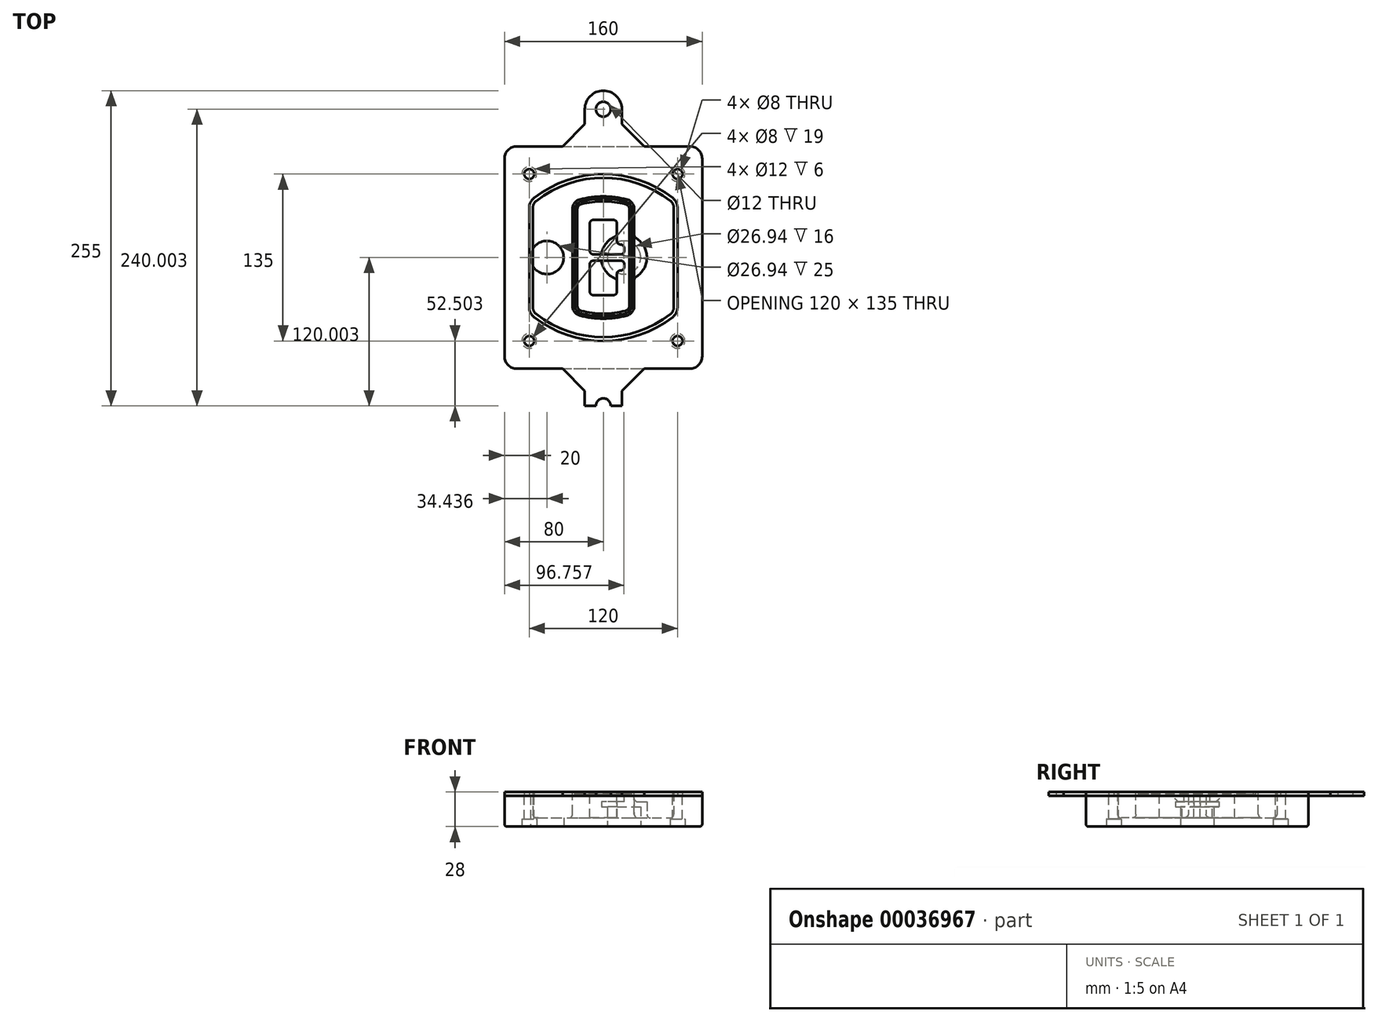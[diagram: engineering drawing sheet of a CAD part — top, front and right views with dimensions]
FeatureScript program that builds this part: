
annotation { "Feature Type Name" : "Feature", "Feature Type Description" : "" }
export const myFeature = defineFeature(function(context is Context, id is Id, definition is map)
    precondition{}
    {
        {
            var Q0;
            Q0=qCreatedBy(makeId("Top.planeOp"),FACE);
            var sketch = newSketch(context, id + "F0", { "sketchPlane" : qUnion([Q0])});
            skPoint(sketch, "E0.rect.middle", {"position": v(0, 0) * mm});
            skLineSegment(sketch, "E1.bottom", {"start": v(24.05, 28.38) * mm, "end": v(164.05, 28.38) * mm});
            skLineSegment(sketch, "E1.top", {"start": v(24.05, 208.38) * mm, "end": v(164.05, 208.38) * mm});
            skLineSegment(sketch, "E1.left", {"start": v(14.05, 38.38) * mm, "end": v(14.05, 198.38) * mm});
            skLineSegment(sketch, "E1.right", {"start": v(174.05, 38.38) * mm, "end": v(174.05, 198.38) * mm});
            skLineSegment(sketch, "E2", {"start": v(14.05, 208.38) * mm, "end": v(174.05, 28.38) * mm, "construction": true});
            skLineSegment(sketch, "E3", {"start": v(174.05, 208.38) * mm, "end": v(14.05, 28.38) * mm, "construction": true});
            skCircle(sketch, "E4", {"center": v(34.05, 185.88) * mm, "radius": 4 * mm});
            skCircle(sketch, "E5", {"center": v(154.05, 185.88) * mm, "radius": 4 * mm});
            skCircle(sketch, "E6", {"center": v(154.05, 50.88) * mm, "radius": 4 * mm});
            skCircle(sketch, "E7", {"center": v(34.05, 50.88) * mm, "radius": 4 * mm});
            skLineSegment(sketch, "E8", {"start": v(34.05, 185.88) * mm, "end": v(154.05, 185.88) * mm, "construction": true});
            skLineSegment(sketch, "E9", {"start": v(154.05, 185.88) * mm, "end": v(154.05, 50.88) * mm, "construction": true});
            skLineSegment(sketch, "E10", {"start": v(154.05, 50.88) * mm, "end": v(34.05, 50.88) * mm, "construction": true});
            skLineSegment(sketch, "E11", {"start": v(34.05, 50.88) * mm, "end": v(34.05, 185.88) * mm, "construction": true});
            skLineSegment(sketch, "E12", {"start": v(34.05, 158.68) * mm, "end": v(34.05, 78.09) * mm});
            skLineSegment(sketch, "E13", {"start": v(154.05, 158.68) * mm, "end": v(154.05, 78.09) * mm});
            skArc(sketch, "E14", {"start": v(150.2, 166.56) * mm, "mid": v(94.05, 185.88) * mm, "end": v(37.9, 166.56) * mm});
            skArc(sketch, "E15", {"start": v(37.9, 70.2) * mm, "mid": v(94.05, 50.88) * mm, "end": v(150.2, 70.2) * mm});
            skLineSegment(sketch, "E16", {"start": v(34.05, 118.38) * mm, "end": v(154.05, 118.38) * mm, "construction": true});
            skPoint(sketch, "E17.visualSharp", {"position": v(34.05, 73.38) * mm});
            skArc(sketch, "E17.filletArc", {"start": v(34.05, 78.09) * mm, "mid": v(35.06, 73.7) * mm, "end": v(37.9, 70.2) * mm});
            skPoint(sketch, "E18.visualSharp", {"position": v(34.05, 163.38) * mm});
            skArc(sketch, "E18.filletArc", {"start": v(37.9, 166.56) * mm, "mid": v(35.06, 163.06) * mm, "end": v(34.05, 158.68) * mm});
            skPoint(sketch, "E19.visualSharp", {"position": v(154.05, 163.38) * mm});
            skArc(sketch, "E19.filletArc", {"start": v(154.05, 158.68) * mm, "mid": v(153.04, 163.06) * mm, "end": v(150.2, 166.56) * mm});
            skPoint(sketch, "E20.visualSharp", {"position": v(154.05, 73.38) * mm});
            skArc(sketch, "E20.filletArc", {"start": v(150.2, 70.2) * mm, "mid": v(153.04, 73.7) * mm, "end": v(154.05, 78.09) * mm});
            skPoint(sketch, "E21.visualSharp", {"position": v(14.05, 208.38) * mm});
            skArc(sketch, "E21.filletArc", {"start": v(24.05, 208.38) * mm, "mid": v(16.98, 205.45) * mm, "end": v(14.05, 198.38) * mm});
            skPoint(sketch, "E22.visualSharp", {"position": v(174.05, 208.38) * mm});
            skArc(sketch, "E22.filletArc", {"start": v(174.05, 198.38) * mm, "mid": v(171.12, 205.45) * mm, "end": v(164.05, 208.38) * mm});
            skPoint(sketch, "E23.visualSharp", {"position": v(174.05, 28.38) * mm});
            skArc(sketch, "E23.filletArc", {"start": v(164.05, 28.38) * mm, "mid": v(171.12, 31.31) * mm, "end": v(174.05, 38.38) * mm});
            skPoint(sketch, "E24.visualSharp", {"position": v(14.05, 28.38) * mm});
            skArc(sketch, "E24.filletArc", {"start": v(14.05, 38.38) * mm, "mid": v(16.98, 31.31) * mm, "end": v(24.05, 28.38) * mm});
            skArc(sketch, "E25.0", {"start": v(151.05, 158.68) * mm, "mid": v(150.34, 161.75) * mm, "end": v(148.36, 164.2) * mm});
            skLineSegment(sketch, "E25.1", {"start": v(151.05, 158.68) * mm, "end": v(151.05, 78.09) * mm});
            skArc(sketch, "E25.2", {"start": v(148.36, 72.57) * mm, "mid": v(150.34, 75.02) * mm, "end": v(151.05, 78.09) * mm});
            skArc(sketch, "E25.3", {"start": v(39.74, 72.57) * mm, "mid": v(94.05, 53.88) * mm, "end": v(148.36, 72.57) * mm});
            skArc(sketch, "E25.4", {"start": v(37.05, 78.09) * mm, "mid": v(37.76, 75.02) * mm, "end": v(39.74, 72.57) * mm});
            skArc(sketch, "E25.5", {"start": v(148.36, 164.2) * mm, "mid": v(94.05, 182.88) * mm, "end": v(39.74, 164.2) * mm});
            skLineSegment(sketch, "E25.6", {"start": v(37.05, 158.68) * mm, "end": v(37.05, 78.09) * mm});
            skArc(sketch, "E25.7", {"start": v(39.74, 164.2) * mm, "mid": v(37.76, 161.75) * mm, "end": v(37.05, 158.68) * mm});
            skArc(sketch, "E26.0", {"start": v(35.43, 169.71) * mm, "mid": v(31.47, 164.82) * mm, "end": v(30.05, 158.68) * mm});
            skArc(sketch, "E26.1", {"start": v(152.67, 169.71) * mm, "mid": v(94.05, 189.88) * mm, "end": v(35.43, 169.71) * mm});
            skArc(sketch, "E26.2", {"start": v(158.05, 158.68) * mm, "mid": v(156.63, 164.82) * mm, "end": v(152.67, 169.71) * mm});
            skLineSegment(sketch, "E26.3", {"start": v(158.05, 158.68) * mm, "end": v(158.05, 78.09) * mm});
            skArc(sketch, "E26.4", {"start": v(152.67, 67.05) * mm, "mid": v(156.63, 71.95) * mm, "end": v(158.05, 78.09) * mm});
            skLineSegment(sketch, "E26.5", {"start": v(30.05, 158.68) * mm, "end": v(30.05, 78.09) * mm});
            skArc(sketch, "E26.6", {"start": v(35.43, 67.05) * mm, "mid": v(94.05, 46.88) * mm, "end": v(152.67, 67.05) * mm});
            skArc(sketch, "E26.7", {"start": v(30.05, 78.09) * mm, "mid": v(31.47, 71.95) * mm, "end": v(35.43, 67.05) * mm});
            skSolve(sketch);
        }
        {
            var Q0;
            Q0=makeQuery(id+"F0.imprint","IMPRINT",FACE,{"disambiguationData":[TD([[makeQuery(id+"F0.imprint","IMPRINT",EDGE,{"derivedFrom":sQuery(id+"F0.wireOp",EDGE,"E1.bottom")}),1.0]])]});
            var Q1;
            Q1=makeQuery(id+"F0.imprint","IMPRINT",FACE,{"disambiguationData":[TD([[makeQuery(id+"F0.imprint","IMPRINT",EDGE,{"derivedFrom":sQuery(id+"F0.wireOp",EDGE,"E12")}),1.0]])]});
            var Q2;
            Q2=makeQuery(id+"F0.imprint","IMPRINT",FACE,{"disambiguationData":[TD([[makeQuery(id+"F0.imprint","IMPRINT",EDGE,{"derivedFrom":sQuery(id+"F0.wireOp",EDGE,"E25.0")}),1.0]])]});
            var Q3;
            Q3=makeQuery(id+"F0.imprint","IMPRINT",FACE,{"disambiguationData":[TD([[makeQuery(id+"F0.imprint","IMPRINT",EDGE,{"derivedFrom":sQuery(id+"F0.wireOp",EDGE,"E12")}),-1.0]])]});
            extrude(context, id + "F1", {"entities" : qUnion([Q0, Q1, Q2, Q3]), "oppositeDirection" : true, "depth" : 25 * mm});
        }
        {
            var Q0;
            Q0=makeQuery(id+"F0.imprint","IMPRINT",FACE,{"disambiguationData":[TD([[makeQuery(id+"F0.imprint","IMPRINT",EDGE,{"derivedFrom":sQuery(id+"F0.wireOp",EDGE,"E12")}),1.0]])]});
            extrude(context, id + "F2", {"entities" : qUnion([Q0]), "operationType" : NewBodyOperationType.ADD, "depth" : 3 * mm});
        }
        {
            var Q0;
            Q0=makeQuery(id+"F0.imprint","IMPRINT",FACE,{"disambiguationData":[TD([[makeQuery(id+"F0.imprint","IMPRINT",EDGE,{"derivedFrom":sQuery(id+"F0.wireOp",EDGE,"E25.0")}),1.0]])]});
            extrude(context, id + "F3", {"entities" : qUnion([Q0]), "operationType" : NewBodyOperationType.REMOVE, "oppositeDirection" : true, "depth" : 18 * mm});
        }
        {
            var Q0;
            Q0=makeQuery(id+"F2.opExtrude","CAP_FACE",FACE,{"disambiguationData":[OSD([sQuery(id+"F0.wireOp",EDGE,"E12"),sQuery(id+"F0.wireOp",EDGE,"E13"),sQuery(id+"F0.wireOp",EDGE,"E14"),sQuery(id+"F0.wireOp",EDGE,"E15"),sQuery(id+"F0.wireOp",EDGE,"E17.filletArc"),sQuery(id+"F0.wireOp",EDGE,"E18.filletArc"),sQuery(id+"F0.wireOp",EDGE,"E19.filletArc"),sQuery(id+"F0.wireOp",EDGE,"E20.filletArc"),sQuery(id+"F0.wireOp",EDGE,"E25.0"),sQuery(id+"F0.wireOp",EDGE,"E25.1"),sQuery(id+"F0.wireOp",EDGE,"E25.2"),sQuery(id+"F0.wireOp",EDGE,"E25.3"),sQuery(id+"F0.wireOp",EDGE,"E25.4"),sQuery(id+"F0.wireOp",EDGE,"E25.5"),sQuery(id+"F0.wireOp",EDGE,"E25.6"),sQuery(id+"F0.wireOp",EDGE,"E25.7")])],"isStart":false});
            var sketch = newSketch(context, id + "F4", { "sketchPlane" : qUnion([Q0])});
            skArc(sketch, "E27.0", {"start": v(74.97, 71.41) * mm, "mid": v(94.05, 68.88) * mm, "end": v(113.13, 71.41) * mm});
            skArc(sketch, "E28.0", {"start": v(113.13, 165.35) * mm, "mid": v(94.05, 167.88) * mm, "end": v(74.97, 165.35) * mm});
            skLineSegment(sketch, "E29", {"start": v(69.05, 157.63) * mm, "end": v(69.05, 79.14) * mm});
            skLineSegment(sketch, "E30", {"start": v(119.05, 157.63) * mm, "end": v(119.05, 79.14) * mm});
            skLineSegment(sketch, "E31", {"start": v(69.05, 163.48) * mm, "end": v(119.05, 163.48) * mm, "construction": true});
            skLineSegment(sketch, "E32", {"start": v(69.05, 73.28) * mm, "end": v(119.05, 73.28) * mm, "construction": true});
            skPoint(sketch, "E33.visualSharp", {"position": v(69.05, 163.48) * mm});
            skArc(sketch, "E33.filletArc", {"start": v(74.97, 165.35) * mm, "mid": v(70.7, 162.5) * mm, "end": v(69.05, 157.63) * mm});
            skPoint(sketch, "E34.visualSharp", {"position": v(119.05, 163.48) * mm});
            skArc(sketch, "E34.filletArc", {"start": v(119.05, 157.63) * mm, "mid": v(117.4, 162.5) * mm, "end": v(113.13, 165.35) * mm});
            skPoint(sketch, "E35.visualSharp", {"position": v(119.05, 73.28) * mm});
            skArc(sketch, "E35.filletArc", {"start": v(113.13, 71.41) * mm, "mid": v(117.4, 74.27) * mm, "end": v(119.05, 79.14) * mm});
            skPoint(sketch, "E36.visualSharp", {"position": v(69.05, 73.28) * mm});
            skArc(sketch, "E36.filletArc", {"start": v(69.05, 79.14) * mm, "mid": v(70.7, 74.27) * mm, "end": v(74.97, 71.41) * mm});
            skArc(sketch, "E37.0", {"start": v(148.36, 164.2) * mm, "mid": v(94.05, 182.88) * mm, "end": v(39.74, 164.2) * mm});
            skArc(sketch, "E37.1", {"start": v(39.74, 164.2) * mm, "mid": v(37.76, 161.75) * mm, "end": v(37.05, 158.68) * mm});
            skLineSegment(sketch, "E37.2", {"start": v(37.05, 158.68) * mm, "end": v(37.05, 78.09) * mm});
            skArc(sketch, "E37.3", {"start": v(37.05, 78.09) * mm, "mid": v(37.76, 75.02) * mm, "end": v(39.74, 72.57) * mm});
            skArc(sketch, "E37.4", {"start": v(39.74, 72.57) * mm, "mid": v(94.05, 53.88) * mm, "end": v(148.36, 72.57) * mm});
            skArc(sketch, "E37.5", {"start": v(148.36, 72.57) * mm, "mid": v(150.34, 75.02) * mm, "end": v(151.05, 78.09) * mm});
            skLineSegment(sketch, "E37.6", {"start": v(151.05, 158.68) * mm, "end": v(151.05, 78.09) * mm});
            skArc(sketch, "E37.7", {"start": v(151.05, 158.68) * mm, "mid": v(150.34, 161.75) * mm, "end": v(148.36, 164.2) * mm});
            skLineSegment(sketch, "E38.0", {"start": v(117.05, 157.63) * mm, "end": v(117.05, 79.14) * mm});
            skArc(sketch, "E38.1", {"start": v(112.61, 73.34) * mm, "mid": v(115.81, 75.49) * mm, "end": v(117.05, 79.14) * mm});
            skArc(sketch, "E38.2", {"start": v(75.49, 73.34) * mm, "mid": v(94.05, 70.88) * mm, "end": v(112.61, 73.34) * mm});
            skArc(sketch, "E38.3", {"start": v(71.05, 79.14) * mm, "mid": v(72.29, 75.49) * mm, "end": v(75.49, 73.34) * mm});
            skLineSegment(sketch, "E38.4", {"start": v(71.05, 157.63) * mm, "end": v(71.05, 79.14) * mm});
            skArc(sketch, "E38.5", {"start": v(117.05, 157.63) * mm, "mid": v(115.81, 161.28) * mm, "end": v(112.61, 163.42) * mm});
            skArc(sketch, "E38.6", {"start": v(75.49, 163.42) * mm, "mid": v(72.29, 161.28) * mm, "end": v(71.05, 157.63) * mm});
            skArc(sketch, "E38.7", {"start": v(112.61, 163.42) * mm, "mid": v(94.05, 165.88) * mm, "end": v(75.49, 163.42) * mm});
            skArc(sketch, "E39.0", {"start": v(115.05, 157.63) * mm, "mid": v(114.23, 160.06) * mm, "end": v(112.1, 161.5) * mm});
            skLineSegment(sketch, "E39.1", {"start": v(115.05, 157.63) * mm, "end": v(115.05, 79.14) * mm});
            skArc(sketch, "E39.2", {"start": v(112.1, 75.27) * mm, "mid": v(114.23, 76.7) * mm, "end": v(115.05, 79.14) * mm});
            skArc(sketch, "E39.3", {"start": v(76, 75.27) * mm, "mid": v(94.05, 72.88) * mm, "end": v(112.1, 75.27) * mm});
            skArc(sketch, "E39.4", {"start": v(73.05, 79.14) * mm, "mid": v(73.87, 76.7) * mm, "end": v(76, 75.27) * mm});
            skArc(sketch, "E39.5", {"start": v(112.1, 161.5) * mm, "mid": v(94.05, 163.88) * mm, "end": v(76, 161.5) * mm});
            skLineSegment(sketch, "E39.6", {"start": v(73.05, 157.63) * mm, "end": v(73.05, 79.14) * mm});
            skArc(sketch, "E39.7", {"start": v(76, 161.5) * mm, "mid": v(73.87, 160.06) * mm, "end": v(73.05, 157.63) * mm});
            skLineSegment(sketch, "E40", {"start": v(69.05, 118.38) * mm, "end": v(119.05, 118.38) * mm, "construction": true});
            skLineSegment(sketch, "E41", {"start": v(83.05, 123.88) * mm, "end": v(83.05, 145.88) * mm});
            skLineSegment(sketch, "E42", {"start": v(86.05, 148.88) * mm, "end": v(102.05, 148.88) * mm});
            skLineSegment(sketch, "E43", {"start": v(105.05, 145.88) * mm, "end": v(105.05, 131.88) * mm});
            skLineSegment(sketch, "E44", {"start": v(108.05, 128.88) * mm, "end": v(108.05, 128.88) * mm});
            skLineSegment(sketch, "E45", {"start": v(111.05, 125.88) * mm, "end": v(111.05, 123.88) * mm});
            skLineSegment(sketch, "E46", {"start": v(108.05, 120.88) * mm, "end": v(86.05, 120.88) * mm});
            skPoint(sketch, "E47.visualSharp", {"position": v(83.05, 148.88) * mm});
            skArc(sketch, "E47.filletArc", {"start": v(86.05, 148.88) * mm, "mid": v(83.93, 148) * mm, "end": v(83.05, 145.88) * mm});
            skPoint(sketch, "E48.visualSharp", {"position": v(105.05, 148.88) * mm});
            skArc(sketch, "E48.filletArc", {"start": v(105.05, 145.88) * mm, "mid": v(104.17, 148) * mm, "end": v(102.05, 148.88) * mm});
            skPoint(sketch, "E49.visualSharp", {"position": v(105.05, 128.88) * mm});
            skArc(sketch, "E49.filletArc", {"start": v(105.05, 131.88) * mm, "mid": v(105.93, 129.76) * mm, "end": v(108.05, 128.88) * mm});
            skPoint(sketch, "E50.visualSharp", {"position": v(111.05, 128.88) * mm});
            skArc(sketch, "E50.filletArc", {"start": v(111.05, 125.88) * mm, "mid": v(110.17, 128) * mm, "end": v(108.05, 128.88) * mm});
            skPoint(sketch, "E51.visualSharp", {"position": v(111.05, 120.88) * mm});
            skArc(sketch, "E51.filletArc", {"start": v(108.05, 120.88) * mm, "mid": v(110.17, 121.76) * mm, "end": v(111.05, 123.88) * mm});
            skPoint(sketch, "E52.visualSharp", {"position": v(83.05, 120.88) * mm});
            skArc(sketch, "E52.filletArc", {"start": v(83.05, 123.88) * mm, "mid": v(83.93, 121.76) * mm, "end": v(86.05, 120.88) * mm});
            skLineSegment(sketch, "E53.0.MirrorCS", {"start": v(108.05, 115.88) * mm, "end": v(86.05, 115.88) * mm});
            skArc(sketch, "E54.0.MirrorCS", {"start": v(83.05, 112.88) * mm, "mid": v(83.93, 115) * mm, "end": v(86.05, 115.88) * mm});
            skLineSegment(sketch, "E55.0.MirrorCS", {"start": v(83.05, 112.88) * mm, "end": v(83.05, 90.88) * mm});
            skArc(sketch, "E56.0.MirrorCS", {"start": v(86.05, 87.88) * mm, "mid": v(83.93, 88.76) * mm, "end": v(83.05, 90.88) * mm});
            skLineSegment(sketch, "E57.0.MirrorCS", {"start": v(86.05, 87.88) * mm, "end": v(102.05, 87.88) * mm});
            skArc(sketch, "E58.0.MirrorCS", {"start": v(105.05, 90.88) * mm, "mid": v(104.17, 88.76) * mm, "end": v(102.05, 87.88) * mm});
            skLineSegment(sketch, "E59.0.MirrorCS", {"start": v(105.05, 90.88) * mm, "end": v(105.05, 104.88) * mm});
            skArc(sketch, "E60.0.MirrorCS", {"start": v(105.05, 104.88) * mm, "mid": v(105.93, 107) * mm, "end": v(108.05, 107.88) * mm});
            skArc(sketch, "E61.0.MirrorCS", {"start": v(111.05, 110.88) * mm, "mid": v(110.17, 108.76) * mm, "end": v(108.05, 107.88) * mm});
            skLineSegment(sketch, "E62.0.MirrorCS", {"start": v(111.05, 110.88) * mm, "end": v(111.05, 112.88) * mm});
            skArc(sketch, "E63.0.MirrorCS", {"start": v(108.05, 115.88) * mm, "mid": v(110.17, 115) * mm, "end": v(111.05, 112.88) * mm});
            skSolve(sketch);
        }
        {
            var Q0;
            Q0=makeQuery(id+"F4.imprint","IMPRINT",FACE,{"disambiguationData":[TD([[makeQuery(id+"F4.imprint","IMPRINT",EDGE,{"derivedFrom":sQuery(id+"F4.wireOp",EDGE,"E27.0")}),1.0]])]});
            var Q1;
            Q1=makeQuery(id+"F4.imprint","IMPRINT",FACE,{"disambiguationData":[TD([[makeQuery(id+"F4.imprint","IMPRINT",EDGE,{"derivedFrom":sQuery(id+"F4.wireOp",EDGE,"E38.0")}),-1.0]])]});
            var Q2;
            Q2=makeQuery(id+"F4.imprint","IMPRINT",FACE,{"disambiguationData":[TD([[makeQuery(id+"F4.imprint","IMPRINT",EDGE,{"derivedFrom":sQuery(id+"F4.wireOp",EDGE,"E39.0")}),1.0]])]});
            extrude(context, id + "F5", {"entities" : qUnion([Q0, Q1, Q2]), "operationType" : NewBodyOperationType.ADD, "endBound" : BoundingType.UP_TO_NEXT, "oppositeDirection" : true, "depth" : 25 * mm});
        }
        {
            var Q0;
            Q0=makeQuery(id+"F4.imprint","IMPRINT",FACE,{"disambiguationData":[TD([[makeQuery(id+"F4.imprint","IMPRINT",EDGE,{"derivedFrom":sQuery(id+"F4.wireOp",EDGE,"E38.0")}),-1.0]])]});
            extrude(context, id + "F6", {"entities" : qUnion([Q0]), "operationType" : NewBodyOperationType.REMOVE, "oppositeDirection" : true, "depth" : 2 * mm});
        }
        {
            var Q0;
            Q0=makeQuery(id+"F1.opExtrude","CAP_FACE",FACE,{"disambiguationData":[OSD([sQuery(id+"F0.wireOp",EDGE,"E1.bottom"),sQuery(id+"F0.wireOp",EDGE,"E1.top"),sQuery(id+"F0.wireOp",EDGE,"E1.left"),sQuery(id+"F0.wireOp",EDGE,"E1.right"),sQuery(id+"F0.wireOp",EDGE,"E4"),sQuery(id+"F0.wireOp",EDGE,"E5"),sQuery(id+"F0.wireOp",EDGE,"E6"),sQuery(id+"F0.wireOp",EDGE,"E7"),sQuery(id+"F0.wireOp",EDGE,"E21.filletArc"),sQuery(id+"F0.wireOp",EDGE,"E22.filletArc"),sQuery(id+"F0.wireOp",EDGE,"E23.filletArc"),sQuery(id+"F0.wireOp",EDGE,"E24.filletArc")])],"isStart":false});
            var sketch = newSketch(context, id + "F7", { "sketchPlane" : qUnion([Q0])});
            skCircle(sketch, "E64", {"center": v(110.8, -118.38) * mm, "radius": 13.47 * mm});
            skCircle(sketch, "E65", {"center": v(48.49, -118.38) * mm, "radius": 13.47 * mm});
            skLineSegment(sketch, "E66", {"start": v(174.05, -118.38) * mm, "end": v(14.05, -118.38) * mm});
            skCircle(sketch, "E67", {"center": v(110.8, -118.38) * mm, "radius": 18.47 * mm});
            skCircle(sketch, "E68", {"center": v(154.05, -185.88) * mm, "radius": 6 * mm});
            skCircle(sketch, "E69", {"center": v(34.05, -185.88) * mm, "radius": 6 * mm});
            skCircle(sketch, "E70", {"center": v(34.05, -50.88) * mm, "radius": 6 * mm});
            skCircle(sketch, "E71", {"center": v(154.05, -50.88) * mm, "radius": 6 * mm});
            skSolve(sketch);
        }
        {
            var Q0;
            {var subQ1=sQuery(id+"F7.wireOp",EDGE,"E66");var subQ4=sQuery(id+"F7.wireOp",EDGE,"E64");var subQ6=makeQuery(id+"F7.imprint","INTERSECT",VERTEX,{"disambiguationData":[OD(0.0)],"derivedFrom":[subQ4,subQ1]});Q0=makeQuery(id+"F7.imprint","IMPRINT",FACE,{"disambiguationData":[TD([[makeQuery(id+"F7.imprint","IMPRINT",EDGE,{"disambiguationData":[TD([[subQ6,-1.0]])],"derivedFrom":subQ4}),-1.0]])]});}
            var Q1;
            {var subQ0=sQuery(id+"F7.wireOp",EDGE,"E66");var subQ1=sQuery(id+"F7.wireOp",EDGE,"E64");var subQ3=makeQuery(id+"F7.imprint","INTERSECT",VERTEX,{"disambiguationData":[OD(0.0)],"derivedFrom":[subQ1,subQ0]});Q1=makeQuery(id+"F7.imprint","IMPRINT",FACE,{"disambiguationData":[TD([[makeQuery(id+"F7.imprint","IMPRINT",EDGE,{"disambiguationData":[TD([[subQ3,-1.0]])],"derivedFrom":subQ1}),1.0]])]});}
            var Q2;
            {var subQ0=sQuery(id+"F7.wireOp",EDGE,"E66");var subQ1=sQuery(id+"F7.wireOp",EDGE,"E64");var subQ3=makeQuery(id+"F7.imprint","INTERSECT",VERTEX,{"disambiguationData":[OD(0.0)],"derivedFrom":[subQ1,subQ0]});Q2=makeQuery(id+"F7.imprint","IMPRINT",FACE,{"disambiguationData":[TD([[makeQuery(id+"F7.imprint","IMPRINT",EDGE,{"disambiguationData":[TD([[subQ3,1.0]])],"derivedFrom":subQ1}),1.0]])]});}
            var Q3;
            {var subQ1=sQuery(id+"F7.wireOp",EDGE,"E66");var subQ4=sQuery(id+"F7.wireOp",EDGE,"E64");var subQ6=makeQuery(id+"F7.imprint","INTERSECT",VERTEX,{"disambiguationData":[OD(0.0)],"derivedFrom":[subQ4,subQ1]});Q3=makeQuery(id+"F7.imprint","IMPRINT",FACE,{"disambiguationData":[TD([[makeQuery(id+"F7.imprint","IMPRINT",EDGE,{"disambiguationData":[TD([[subQ6,1.0]])],"derivedFrom":subQ4}),-1.0]])]});}
            extrude(context, id + "F8", {"entities" : qUnion([Q0, Q1, Q2, Q3]), "operationType" : NewBodyOperationType.ADD, "oppositeDirection" : true, "depth" : 20 * mm});
        }
        {
            var Q0;
            {var subQ0=sQuery(id+"F7.wireOp",EDGE,"E66");var subQ1=sQuery(id+"F7.wireOp",EDGE,"E64");var subQ3=makeQuery(id+"F7.imprint","INTERSECT",VERTEX,{"disambiguationData":[OD(0.0)],"derivedFrom":[subQ1,subQ0]});Q0=makeQuery(id+"F7.imprint","IMPRINT",FACE,{"disambiguationData":[TD([[makeQuery(id+"F7.imprint","IMPRINT",EDGE,{"disambiguationData":[TD([[subQ3,-1.0]])],"derivedFrom":subQ1}),1.0]])]});}
            var Q1;
            {var subQ0=sQuery(id+"F7.wireOp",EDGE,"E66");var subQ1=sQuery(id+"F7.wireOp",EDGE,"E64");var subQ3=makeQuery(id+"F7.imprint","INTERSECT",VERTEX,{"disambiguationData":[OD(0.0)],"derivedFrom":[subQ1,subQ0]});Q1=makeQuery(id+"F7.imprint","IMPRINT",FACE,{"disambiguationData":[TD([[makeQuery(id+"F7.imprint","IMPRINT",EDGE,{"disambiguationData":[TD([[subQ3,1.0]])],"derivedFrom":subQ1}),1.0]])]});}
            extrude(context, id + "F9", {"entities" : qUnion([Q0, Q1]), "operationType" : NewBodyOperationType.REMOVE, "oppositeDirection" : true, "depth" : 16 * mm});
        }
        {
            var Q0;
            {var subQ0=sQuery(id+"F7.wireOp",EDGE,"E66");var subQ1=sQuery(id+"F7.wireOp",EDGE,"E65");var subQ3=makeQuery(id+"F7.imprint","INTERSECT",VERTEX,{"disambiguationData":[OD(0.0)],"derivedFrom":[subQ1,subQ0]});Q0=makeQuery(id+"F7.imprint","IMPRINT",FACE,{"disambiguationData":[TD([[makeQuery(id+"F7.imprint","IMPRINT",EDGE,{"disambiguationData":[TD([[subQ3,-1.0]])],"derivedFrom":subQ1}),1.0]])]});}
            var Q1;
            {var subQ0=sQuery(id+"F7.wireOp",EDGE,"E66");var subQ1=sQuery(id+"F7.wireOp",EDGE,"E65");var subQ3=makeQuery(id+"F7.imprint","INTERSECT",VERTEX,{"disambiguationData":[OD(0.0)],"derivedFrom":[subQ1,subQ0]});Q1=makeQuery(id+"F7.imprint","IMPRINT",FACE,{"disambiguationData":[TD([[makeQuery(id+"F7.imprint","IMPRINT",EDGE,{"disambiguationData":[TD([[subQ3,1.0]])],"derivedFrom":subQ1}),1.0]])]});}
            extrude(context, id + "F10", {"entities" : qUnion([Q0, Q1]), "operationType" : NewBodyOperationType.REMOVE, "oppositeDirection" : true, "depth" : 25 * mm});
        }
        {
            var Q0;
            Q0=makeQuery(id+"F7.imprint","IMPRINT",FACE,{"disambiguationData":[TD([[makeQuery(id+"F7.imprint","IMPRINT",EDGE,{"derivedFrom":sQuery(id+"F7.wireOp",EDGE,"E68")}),1.0]])]});
            var Q1;
            Q1=makeQuery(id+"F7.imprint","IMPRINT",FACE,{"disambiguationData":[TD([[makeQuery(id+"F7.imprint","IMPRINT",EDGE,{"derivedFrom":makeQuery(id+"F1.opExtrude","CAP_EDGE",EDGE,{"disambiguationData":[OSD([sQuery(id+"F0.wireOp",EDGE,"E5")])],"isStart":false})}),-1.0]])]});
            var Q2;
            Q2=makeQuery(id+"F7.imprint","IMPRINT",FACE,{"disambiguationData":[TD([[makeQuery(id+"F7.imprint","IMPRINT",EDGE,{"derivedFrom":sQuery(id+"F7.wireOp",EDGE,"E69")}),1.0]])]});
            var Q3;
            Q3=makeQuery(id+"F7.imprint","IMPRINT",FACE,{"disambiguationData":[TD([[makeQuery(id+"F7.imprint","IMPRINT",EDGE,{"derivedFrom":makeQuery(id+"F1.opExtrude","CAP_EDGE",EDGE,{"disambiguationData":[OSD([sQuery(id+"F0.wireOp",EDGE,"E4")])],"isStart":false})}),-1.0]])]});
            var Q4;
            Q4=makeQuery(id+"F7.imprint","IMPRINT",FACE,{"disambiguationData":[TD([[makeQuery(id+"F7.imprint","IMPRINT",EDGE,{"derivedFrom":sQuery(id+"F7.wireOp",EDGE,"E70")}),1.0]])]});
            var Q5;
            Q5=makeQuery(id+"F7.imprint","IMPRINT",FACE,{"disambiguationData":[TD([[makeQuery(id+"F7.imprint","IMPRINT",EDGE,{"derivedFrom":makeQuery(id+"F1.opExtrude","CAP_EDGE",EDGE,{"disambiguationData":[OSD([sQuery(id+"F0.wireOp",EDGE,"E7")])],"isStart":false})}),-1.0]])]});
            var Q6;
            Q6=makeQuery(id+"F7.imprint","IMPRINT",FACE,{"disambiguationData":[TD([[makeQuery(id+"F7.imprint","IMPRINT",EDGE,{"derivedFrom":sQuery(id+"F7.wireOp",EDGE,"E71")}),1.0]])]});
            var Q7;
            Q7=makeQuery(id+"F7.imprint","IMPRINT",FACE,{"disambiguationData":[TD([[makeQuery(id+"F7.imprint","IMPRINT",EDGE,{"derivedFrom":makeQuery(id+"F1.opExtrude","CAP_EDGE",EDGE,{"disambiguationData":[OSD([sQuery(id+"F0.wireOp",EDGE,"E6")])],"isStart":false})}),-1.0]])]});
            extrude(context, id + "F11", {"entities" : qUnion([Q0, Q1, Q2, Q3, Q4, Q5, Q6, Q7]), "operationType" : NewBodyOperationType.REMOVE, "oppositeDirection" : true, "depth" : 6 * mm});
        }
        {
            var Q0;
            Q0=makeQuery(id+"F9.boolean.opBoolean","COPY",FACE,{"derivedFrom":makeQuery(id+"F9.opExtrude","CAP_FACE",FACE,{"disambiguationData":[OSD([sQuery(id+"F7.wireOp",EDGE,"E64")])],"isStart":false})});
            var sketch = newSketch(context, id + "F12", { "sketchPlane" : qUnion([Q0])});
            skArc(sketch, "E72.0", {"start": v(105.05, -100.83) * mm, "mid": v(96.62, -106.56) * mm, "end": v(92.5, -115.88) * mm});
            skArc(sketch, "E72.1", {"start": v(92.5, -120.88) * mm, "mid": v(96.62, -130.2) * mm, "end": v(105.05, -135.93) * mm});
            skLineSegment(sketch, "E73", {"start": v(92.5, -120.88) * mm, "end": v(108.05, -120.88) * mm});
            skLineSegment(sketch, "E74.0", {"start": v(108.05, -115.88) * mm, "end": v(92.5, -115.88) * mm});
            skArc(sketch, "E74.1", {"start": v(108.05, -115.88) * mm, "mid": v(110.17, -115) * mm, "end": v(111.05, -112.88) * mm});
            skLineSegment(sketch, "E74.2", {"start": v(111.05, -110.88) * mm, "end": v(111.05, -112.88) * mm});
            skArc(sketch, "E74.3", {"start": v(111.05, -110.88) * mm, "mid": v(110.17, -108.76) * mm, "end": v(108.05, -107.88) * mm});
            skArc(sketch, "E74.4", {"start": v(105.05, -104.88) * mm, "mid": v(105.93, -107) * mm, "end": v(108.05, -107.88) * mm});
            skLineSegment(sketch, "E74.5", {"start": v(105.05, -100.83) * mm, "end": v(105.05, -104.88) * mm});
            skLineSegment(sketch, "E74.7", {"start": v(108.05, -120.88) * mm, "end": v(92.5, -120.88) * mm});
            skArc(sketch, "E74.8", {"start": v(108.05, -120.88) * mm, "mid": v(110.17, -121.76) * mm, "end": v(111.05, -123.88) * mm});
            skLineSegment(sketch, "E74.9", {"start": v(111.05, -125.88) * mm, "end": v(111.05, -123.88) * mm});
            skArc(sketch, "E74.10", {"start": v(111.05, -125.88) * mm, "mid": v(110.17, -128) * mm, "end": v(108.05, -128.88) * mm});
            skArc(sketch, "E74.11", {"start": v(105.05, -131.88) * mm, "mid": v(105.93, -129.76) * mm, "end": v(108.05, -128.88) * mm});
            skLineSegment(sketch, "E74.12", {"start": v(105.05, -135.93) * mm, "end": v(105.05, -131.88) * mm});
            skPoint(sketch, "E75.orphan", {"position": v(105.05, -145.88) * mm});
            skPoint(sketch, "E76.orphan", {"position": v(86.05, -120.88) * mm});
            skPoint(sketch, "E77.orphan", {"position": v(86.05, -115.88) * mm});
            skPoint(sketch, "E78.orphan", {"position": v(105.05, -90.88) * mm});
            skSolve(sketch);
        }
        {
            var Q0;
            {var subQ7=sQuery(id+"F12.wireOp",EDGE,"E72.0");var subQ14=sQuery(id+"F12.wireOp",EDGE,"E72.1");var subQ16=sQuery(id+"F12.wireOp",EDGE,"E74.1");var subQ18=sQuery(id+"F12.wireOp",EDGE,"E74.8");Q0=qUnion([makeQuery(id+"F12.imprint","IMPRINT",FACE,{"disambiguationData":[TD([[makeQuery(id+"F12.imprint","IMPRINT",EDGE,{"derivedFrom":subQ7}),1.0]])]}),makeQuery(id+"F12.imprint","IMPRINT",FACE,{"disambiguationData":[TD([[makeQuery(id+"F12.imprint","IMPRINT",EDGE,{"derivedFrom":subQ14}),1.0]])]}),makeQuery(id+"F12.imprint","IMPRINT",FACE,{"disambiguationData":[TD([[makeQuery(id+"F12.imprint","IMPRINT",EDGE,{"derivedFrom":subQ16}),1.0]])]}),makeQuery(id+"F12.imprint","IMPRINT",FACE,{"disambiguationData":[TD([[makeQuery(id+"F12.imprint","IMPRINT",EDGE,{"derivedFrom":subQ18}),-1.0]])]})]);}
            var Q1;
            Q1=makeQuery(id+"F5.boolean.opBoolean","SPLIT",FACE,{"disambiguationData":[TD([makeQuery(id+"F5.opExtrude","SWEPT_FACE",FACE,{"disambiguationData":[OSD([sQuery(id+"F4.wireOp",EDGE,"E41")])]})])],"derivedFrom":makeQuery(id+"F3.boolean.opBoolean","COPY",FACE,{"derivedFrom":makeQuery(id+"F3.opExtrude","CAP_FACE",FACE,{"disambiguationData":[OSD([sQuery(id+"F0.wireOp",EDGE,"E25.0"),sQuery(id+"F0.wireOp",EDGE,"E25.1"),sQuery(id+"F0.wireOp",EDGE,"E25.2"),sQuery(id+"F0.wireOp",EDGE,"E25.3"),sQuery(id+"F0.wireOp",EDGE,"E25.4"),sQuery(id+"F0.wireOp",EDGE,"E25.5"),sQuery(id+"F0.wireOp",EDGE,"E25.6"),sQuery(id+"F0.wireOp",EDGE,"E25.7")])],"isStart":false})})});
            extrude(context, id + "F13", {"entities" : qUnion([Q0]), "operationType" : NewBodyOperationType.REMOVE, "endBound" : BoundingType.UP_TO_SURFACE, "endBoundEntityFace" : qUnion([Q1]), "depth" : 25 * mm});
        }
        {
            var Q0;
            Q0=makeQuery(id+"F3.boolean.opBoolean","COPY",EDGE,{"derivedFrom":makeQuery(id+"F3.opExtrude","CAP_EDGE",EDGE,{"disambiguationData":[OSD([sQuery(id+"F0.wireOp",EDGE,"E25.6")])],"isStart":false})});
            var Q1;
            Q1=makeQuery(id+"F8.boolean.opBoolean","INTERSECT",EDGE,{"derivedFrom":[makeQuery(id+"F5.opExtrude","SWEPT_FACE",FACE,{"disambiguationData":[OSD([sQuery(id+"F4.wireOp",EDGE,"E30")])]}),makeQuery(id+"F8.opExtrude","CAP_FACE",FACE,{"disambiguationData":[OSD([sQuery(id+"F7.wireOp",EDGE,"E67")])],"isStart":false})]});
            var Q2;
            Q2=makeQuery(id+"F8.boolean.opBoolean","INTERSECT",EDGE,{"disambiguationData":[OD(1.0)],"derivedFrom":[makeQuery(id+"F5.opExtrude","SWEPT_FACE",FACE,{"disambiguationData":[OSD([sQuery(id+"F4.wireOp",EDGE,"E30")])]}),makeQuery(id+"F8.opExtrude","SWEPT_FACE",FACE,{"disambiguationData":[OSD([sQuery(id+"F7.wireOp",EDGE,"E67")])]})]});
            var Q3;
            {var subQ0=sQuery(id+"F4.wireOp",EDGE,"E30");Q3=makeQuery(id+"F8.boolean.opBoolean","SPLIT",EDGE,{"disambiguationData":[TD([makeQuery(id+"F5.opExtrude","SWEPT_FACE",FACE,{"disambiguationData":[OSD([sQuery(id+"F4.wireOp",EDGE,"E35.filletArc")])]})])],"derivedFrom":makeQuery(id+"F5.opExtrude","CAP_EDGE",EDGE,{"disambiguationData":[OSD([subQ0])],"isStart":false})});}
            var Q4;
            {var subQ0=sQuery(id+"F0.wireOp",EDGE,"E25.7");var subQ1=sQuery(id+"F0.wireOp",EDGE,"E25.1");var subQ2=sQuery(id+"F0.wireOp",EDGE,"E25.6");var subQ3=sQuery(id+"F0.wireOp",EDGE,"E25.5");var subQ4=sQuery(id+"F0.wireOp",EDGE,"E25.4");var subQ5=sQuery(id+"F0.wireOp",EDGE,"E25.0");var subQ6=sQuery(id+"F0.wireOp",EDGE,"E25.2");var subQ7=sQuery(id+"F0.wireOp",EDGE,"E25.3");Q4=makeQuery(id+"F8.boolean.opBoolean","INTERSECT",EDGE,{"derivedFrom":[makeQuery(id+"F5.boolean.opBoolean","SPLIT",FACE,{"disambiguationData":[TD([makeQuery(id+"F2.opExtrude","SWEPT_FACE",FACE,{"disambiguationData":[OSD([subQ5])]})])],"derivedFrom":makeQuery(id+"F3.boolean.opBoolean","COPY",FACE,{"derivedFrom":makeQuery(id+"F3.opExtrude","CAP_FACE",FACE,{"disambiguationData":[OSD([subQ5,subQ1,subQ6,subQ7,subQ4,subQ3,subQ2,subQ0])],"isStart":false})})}),makeQuery(id+"F8.opExtrude","SWEPT_FACE",FACE,{"disambiguationData":[OSD([sQuery(id+"F7.wireOp",EDGE,"E67")])]})]});}
            var Q5;
            Q5=makeQuery(id+"F8.boolean.opBoolean","INTERSECT",EDGE,{"disambiguationData":[OD(0.0)],"derivedFrom":[makeQuery(id+"F5.opExtrude","SWEPT_FACE",FACE,{"disambiguationData":[OSD([sQuery(id+"F4.wireOp",EDGE,"E30")])]}),makeQuery(id+"F8.opExtrude","SWEPT_FACE",FACE,{"disambiguationData":[OSD([sQuery(id+"F7.wireOp",EDGE,"E67")])]})]});
            fillet(context, id + "F14", {"entities" : qUnion([Q0, Q1, Q2, Q3, Q4, Q5]), "radius" : 3 * mm, "tangentPropagation" : true, "allowEdgeOverflow" : false});
        }
        {
            var Q0;
            Q0=makeQuery(id+"F1.opExtrude","CAP_EDGE",EDGE,{"disambiguationData":[OSD([sQuery(id+"F0.wireOp",EDGE,"E1.bottom")])],"isStart":false});
            fillet(context, id + "F15", {"entities" : qUnion([Q0]), "radius" : 2 * mm, "tangentPropagation" : true, "allowEdgeOverflow" : false});
        }
        {
            var Q0;
            {var subQ0=sQuery(id+"F0.wireOp",EDGE,"E1.bottom");var subQ1=sQuery(id+"F0.wireOp",EDGE,"E1.top");var subQ2=sQuery(id+"F0.wireOp",EDGE,"E1.left");var subQ3=sQuery(id+"F0.wireOp",EDGE,"E1.right");var subQ4=sQuery(id+"F0.wireOp",EDGE,"E4");var subQ5=sQuery(id+"F0.wireOp",EDGE,"E5");var subQ6=sQuery(id+"F0.wireOp",EDGE,"E6");var subQ7=sQuery(id+"F0.wireOp",EDGE,"E7");var subQ8=sQuery(id+"F0.wireOp",EDGE,"E21.filletArc");var subQ9=sQuery(id+"F0.wireOp",EDGE,"E22.filletArc");var subQ10=sQuery(id+"F0.wireOp",EDGE,"E23.filletArc");var subQ11=sQuery(id+"F0.wireOp",EDGE,"E24.filletArc");Q0=makeQuery(id+"F2.boolean.opBoolean","SPLIT",FACE,{"disambiguationData":[TD([makeQuery(id+"F1.opExtrude","SWEPT_FACE",FACE,{"disambiguationData":[OSD([subQ0])]})])],"derivedFrom":makeQuery(id+"F1.opExtrude","CAP_FACE",FACE,{"disambiguationData":[OSD([subQ0,subQ1,subQ2,subQ3,subQ4,subQ5,subQ6,subQ7,subQ8,subQ9,subQ10,subQ11])],"isStart":true})});}
            var sketch = newSketch(context, id + "F16", { "sketchPlane" : qUnion([Q0])});
            skArc(sketch, "E79.1", {"start": v(24.05, 208.38) * mm, "mid": v(16.98, 205.45) * mm, "end": v(14.05, 198.38) * mm});
            skLineSegment(sketch, "E79.2", {"start": v(14.05, 38.38) * mm, "end": v(14.05, 198.38) * mm});
            skArc(sketch, "E79.3", {"start": v(14.05, 38.38) * mm, "mid": v(16.98, 31.31) * mm, "end": v(24.05, 28.38) * mm});
            skLineSegment(sketch, "E79.4", {"start": v(24.05, 28.38) * mm, "end": v(164.05, 28.38) * mm});
            skArc(sketch, "E79.5", {"start": v(164.05, 28.38) * mm, "mid": v(171.12, 31.31) * mm, "end": v(174.05, 38.38) * mm});
            skLineSegment(sketch, "E79.6", {"start": v(174.05, 38.38) * mm, "end": v(174.05, 198.38) * mm});
            skArc(sketch, "E79.7", {"start": v(174.05, 198.38) * mm, "mid": v(171.12, 205.45) * mm, "end": v(164.05, 208.38) * mm});
            skArc(sketch, "E79.8", {"start": v(150.2, 166.56) * mm, "mid": v(94.05, 185.88) * mm, "end": v(37.9, 166.56) * mm});
            skArc(sketch, "E79.9", {"start": v(37.9, 166.56) * mm, "mid": v(35.06, 163.06) * mm, "end": v(34.05, 158.68) * mm});
            skLineSegment(sketch, "E79.10", {"start": v(34.05, 158.68) * mm, "end": v(34.05, 78.09) * mm});
            skArc(sketch, "E79.11", {"start": v(34.05, 78.09) * mm, "mid": v(35.06, 73.7) * mm, "end": v(37.9, 70.2) * mm});
            skArc(sketch, "E79.12", {"start": v(37.9, 70.2) * mm, "mid": v(94.05, 50.88) * mm, "end": v(150.2, 70.2) * mm});
            skArc(sketch, "E79.13", {"start": v(150.2, 70.2) * mm, "mid": v(153.04, 73.7) * mm, "end": v(154.05, 78.09) * mm});
            skLineSegment(sketch, "E79.14", {"start": v(154.05, 158.68) * mm, "end": v(154.05, 78.09) * mm});
            skArc(sketch, "E79.15", {"start": v(154.05, 158.68) * mm, "mid": v(153.04, 163.06) * mm, "end": v(150.2, 166.56) * mm});
            skLineSegment(sketch, "E80.0", {"start": v(24.05, 208.38) * mm, "end": v(164.05, 208.38) * mm});
            skLineSegment(sketch, "E81", {"start": v(94.05, 208.38) * mm, "end": v(94.05, 238.38) * mm, "construction": true});
            skCircle(sketch, "E82", {"center": v(94.05, 238.38) * mm, "radius": 6 * mm});
            skLineSegment(sketch, "E83", {"start": v(61.05, 208.38) * mm, "end": v(79.05, 226.38) * mm});
            skLineSegment(sketch, "E84", {"start": v(79.05, 226.38) * mm, "end": v(79.05, 238.38) * mm});
            skLineSegment(sketch, "E85", {"start": v(127.05, 208.38) * mm, "end": v(109.05, 226.38) * mm});
            skLineSegment(sketch, "E86", {"start": v(109.05, 226.38) * mm, "end": v(109.05, 238.38) * mm});
            skArc(sketch, "E87", {"start": v(109.05, 238.38) * mm, "mid": v(94.05, 253.38) * mm, "end": v(79.05, 238.38) * mm});
            skLineSegment(sketch, "E88", {"start": v(79.05, 238.38) * mm, "end": v(94.05, 238.38) * mm, "construction": true});
            skLineSegment(sketch, "E89", {"start": v(109.05, 238.38) * mm, "end": v(94.05, 238.38) * mm, "construction": true});
            skLineSegment(sketch, "E90", {"start": v(14.05, 118.38) * mm, "end": v(174.05, 118.38) * mm, "construction": true});
            skLineSegment(sketch, "E91.MirrorCS", {"start": v(109.05, 10.38) * mm, "end": v(109.05, -1.62) * mm});
            skLineSegment(sketch, "E92.MirrorCS", {"start": v(94.05, 28.38) * mm, "end": v(94.05, -1.62) * mm});
            skLineSegment(sketch, "E93.MirrorCS", {"start": v(61.05, 28.38) * mm, "end": v(79.05, 10.38) * mm});
            skArc(sketch, "E94.MirrorCS", {"start": v(109.05, -1.62) * mm, "mid": v(94.05, -16.62) * mm, "end": v(79.05, -1.62) * mm});
            skLineSegment(sketch, "E95.MirrorCS", {"start": v(109.05, -1.62) * mm, "end": v(94.05, -1.62) * mm});
            skLineSegment(sketch, "E96.MirrorCS", {"start": v(79.05, -1.62) * mm, "end": v(94.05, -1.62) * mm});
            skLineSegment(sketch, "E97.MirrorCS", {"start": v(79.05, 10.38) * mm, "end": v(79.05, -1.62) * mm});
            skLineSegment(sketch, "E98.MirrorCS", {"start": v(127.05, 28.38) * mm, "end": v(109.05, 10.38) * mm});
            skCircle(sketch, "E99.MirrorC", {"center": v(94.05, -1.62) * mm, "radius": 6 * mm});
            skSolve(sketch);
        }
        {
            var Q0;
            Q0=makeQuery(id+"F16.imprint","IMPRINT",FACE,{"disambiguationData":[TD([[makeQuery(id+"F16.imprint","IMPRINT",EDGE,{"derivedFrom":sQuery(id+"F16.wireOp",EDGE,"E82")}),-1.0]])]});
            var Q1;
            {var subQ6=sQuery(id+"F16.wireOp",EDGE,"E93.MirrorCS");Q1=makeQuery(id+"F16.imprint","IMPRINT",FACE,{"disambiguationData":[TD([[makeQuery(id+"F16.imprint","IMPRINT",EDGE,{"derivedFrom":subQ6}),1.0]])]});}
            var Q2;
            {var subQ6=sQuery(id+"F16.wireOp",EDGE,"E91.MirrorCS");Q2=makeQuery(id+"F16.imprint","IMPRINT",FACE,{"disambiguationData":[TD([[makeQuery(id+"F16.imprint","IMPRINT",EDGE,{"derivedFrom":subQ6}),-1.0]])]});}
            var Q3;
            {var subQ5=sQuery(id+"F16.wireOp",EDGE,"E94.MirrorCS");Q3=makeQuery(id+"F16.imprint","IMPRINT",FACE,{"disambiguationData":[TD([[makeQuery(id+"F16.imprint","IMPRINT",EDGE,{"derivedFrom":subQ5}),-1.0]])]});}
            var Q4;
            {var subQ9=sQuery(id+"F16.wireOp",EDGE,"E79.1");Q4=makeQuery(id+"F16.imprint","IMPRINT",FACE,{"disambiguationData":[TD([[makeQuery(id+"F16.imprint","IMPRINT",EDGE,{"derivedFrom":subQ9}),1.0]])]});}
            var Q5;
            {var subQ0=sQuery(id+"F4.wireOp",EDGE,"E63.0.MirrorCS");var subQ1=sQuery(id+"F4.wireOp",EDGE,"E62.0.MirrorCS");var subQ2=sQuery(id+"F4.wireOp",EDGE,"E61.0.MirrorCS");var subQ3=sQuery(id+"F4.wireOp",EDGE,"E60.0.MirrorCS");var subQ4=sQuery(id+"F4.wireOp",EDGE,"E59.0.MirrorCS");var subQ5=sQuery(id+"F4.wireOp",EDGE,"E58.0.MirrorCS");var subQ6=sQuery(id+"F4.wireOp",EDGE,"E57.0.MirrorCS");var subQ7=sQuery(id+"F4.wireOp",EDGE,"E56.0.MirrorCS");var subQ8=sQuery(id+"F4.wireOp",EDGE,"E55.0.MirrorCS");var subQ9=sQuery(id+"F4.wireOp",EDGE,"E54.0.MirrorCS");var subQ10=sQuery(id+"F4.wireOp",EDGE,"E53.0.MirrorCS");var subQ11=sQuery(id+"F4.wireOp",EDGE,"E52.filletArc");var subQ12=sQuery(id+"F4.wireOp",EDGE,"E45");var subQ13=sQuery(id+"F4.wireOp",EDGE,"E43");var subQ14=sQuery(id+"F4.wireOp",EDGE,"E42");var subQ15=sQuery(id+"F4.wireOp",EDGE,"E41");var subQ16=sQuery(id+"F4.wireOp",EDGE,"E46");var subQ17=sQuery(id+"F4.wireOp",EDGE,"E47.filletArc");var subQ18=sQuery(id+"F4.wireOp",EDGE,"E48.filletArc");var subQ19=sQuery(id+"F4.wireOp",EDGE,"E49.filletArc");var subQ20=sQuery(id+"F4.wireOp",EDGE,"E50.filletArc");var subQ21=sQuery(id+"F4.wireOp",EDGE,"E51.filletArc");Q5=makeQuery(id+"F6.boolean.opBoolean","SPLIT",FACE,{"disambiguationData":[TD([makeQuery(id+"F5.opExtrude","SWEPT_FACE",FACE,{"disambiguationData":[OSD([subQ15])]})])],"derivedFrom":makeQuery(id+"F5.opExtrude","CAP_FACE",FACE,{"disambiguationData":[OSD([sQuery(id+"F4.wireOp",EDGE,"E27.0"),sQuery(id+"F4.wireOp",EDGE,"E28.0"),sQuery(id+"F4.wireOp",EDGE,"E29"),sQuery(id+"F4.wireOp",EDGE,"E30"),sQuery(id+"F4.wireOp",EDGE,"E33.filletArc"),sQuery(id+"F4.wireOp",EDGE,"E34.filletArc"),sQuery(id+"F4.wireOp",EDGE,"E35.filletArc"),sQuery(id+"F4.wireOp",EDGE,"E36.filletArc"),subQ15,subQ14,subQ13,subQ12,subQ16,subQ17,subQ18,subQ19,subQ20,subQ21,subQ11,subQ10,subQ9,subQ8,subQ7,subQ6,subQ5,subQ4,subQ3,subQ2,subQ1,subQ0])],"isStart":true})});}
            extrude(context, id + "F17", {"entities" : qUnion([Q0, Q1, Q2, Q3, Q4]), "endBound" : BoundingType.UP_TO_SURFACE, "endBoundEntityFace" : qUnion([Q5]), "depth" : 25 * mm});
        }
    });
